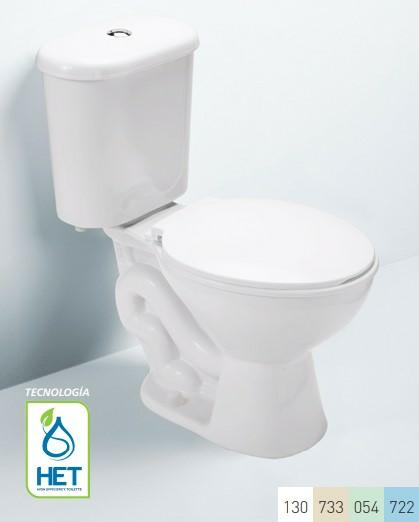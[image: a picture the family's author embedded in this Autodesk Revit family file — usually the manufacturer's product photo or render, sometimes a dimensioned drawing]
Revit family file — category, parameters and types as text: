
# Revit family: BRG-SNT-LVF_FUENTE LUGANO BLANCO v_02
name_source: partatom
category: Aparatos sanitarios
units: mm (PartAtom-declared; Revit-internal decimal feet)

## family parameters
Compartido = Sí
Corte con vacíos al cargar = No
Cota de conector redondo = Diámetro de uso
Número OmniClass = 23.45.00.00
Punto de cálculo de habitación = Sí
Se basa en plano de trabajo = No
Siempre vertical = Sí
Tipo de pieza = Normal
Título OmniClass = Sanitary, Laundry, and Cleaning Equipment

## types (1)
- LAVAMANOS LUGANO
    Conexión AC = Sí
    Conexión AF = Sí
    Conexión de residuos = Sí
    Conexión de ventilación = Sí
    Fabricante = BRIGGS Ecuador
    Imagen de tipo = <Ninguno>
    Modelo = LAVAMANOS LUGANO
    URL = https://www.briggs.com.ec
    _ALT_Basamento = 0.8 m
    _ALT_Eje instalación = 0.6 m
    _EDESA_ Alto en cm = 13.5
    _EDESA_ Ancho en cm = 39.3
    _EDESA_ Categoría = Productos > Sanitarios > Lavamanos > Fuente
    _EDESA_ Certificación = Cumple con norma NTE INEN 3082
    _EDESA_ Color = blanco, bone, cotton
    _EDESA_ Conexión hidráulica = Entrada de agua: tubería ø 1/2" Salida de agua: tubería PVC 50
    _EDESA_ Consumo/capacidad de agua en L = 5.0 litros
    _EDESA_ Descripción = Lavamanos tipo fuente, instalado sobre mueble o mesón, con perforación para grifería monomando.
    _EDESA_ Distancia de instalación en cm (muro terminado) = 0
    _EDESA_ Garantía = De por vida en funcionamiento y acabado de la cerámica sanitaria
    _EDESA_ Manual de instalación = https://www.briggs.com.ec
    _EDESA_ Marca = BRIGGS
    _EDESA_ Materiales = Cerámica Sanitaria
    _EDESA_ Nombre = LAVAMANOS LUGANO
    _EDESA_ Peso en kg = 6.9 kg
    _EDESA_ Productos necesarios para instalación = Grifería, Desagüe 1 1/4", Sifón 1 1/4", Silicón
    _EDESA_ Profundidad en cm = 39.3
    _EDESA_ Sku/código = SS005731___1CW
    _EDESA_ Tipo de instalación = Sobre mueble
